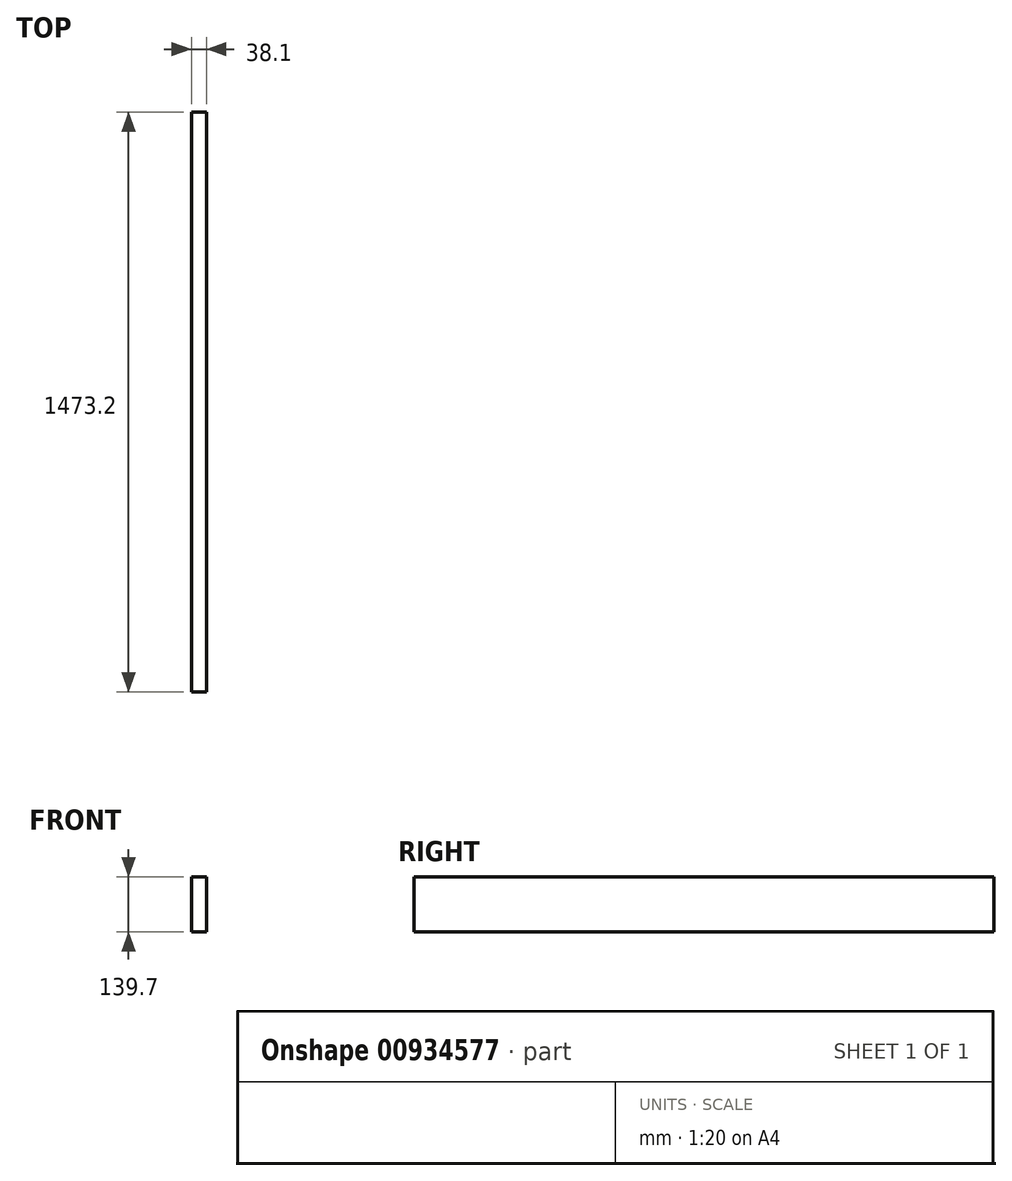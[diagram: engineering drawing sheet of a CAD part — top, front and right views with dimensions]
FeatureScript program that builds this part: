
annotation { "Feature Type Name" : "Feature", "Feature Type Description" : "" }
export const myFeature = defineFeature(function(context is Context, id is Id, definition is map)
    precondition{}
    {
        {
            var Q0;
            Q0=qCreatedBy(makeId("Front.planeOp"),FACE);
            var sketch = newSketch(context, id + "F0", { "sketchPlane" : qUnion([Q0])});
            skLineSegment(sketch, "E0.bottom", {"start": v(0, 0) * mm, "end": v(-38.1, 0) * mm});
            skLineSegment(sketch, "E0.top", {"start": v(0, 139.7) * mm, "end": v(-38.1, 139.7) * mm});
            skLineSegment(sketch, "E0.left", {"start": v(0, 0) * mm, "end": v(0, 139.7) * mm});
            skLineSegment(sketch, "E0.right", {"start": v(-38.1, 0) * mm, "end": v(-38.1, 139.7) * mm});
            skSolve(sketch);
        }
        {
            var Q0;
            Q0=makeQuery(id+"F0.imprint","IMPRINT",FACE,{"disambiguationData":[TD([[makeQuery(id+"F0.imprint","IMPRINT",EDGE,{"derivedFrom":sQuery(id+"F0.wireOp",EDGE,"E0.bottom")}),-1.0]])]});
            extrude(context, id + "F1", {"entities" : qUnion([Q0]), "depth" : 1473.2 * mm, "offsetDistance" : 25.4 * mm});
        }
    });
